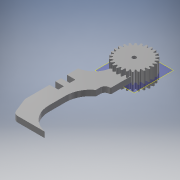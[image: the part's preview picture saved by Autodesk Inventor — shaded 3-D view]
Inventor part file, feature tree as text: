
AUTODESK INVENTOR PART (.ipt)
format: ipt  version: 2017 (Build 210142000, 142)  size: 346,624 bytes
history: native  units: mm (DEFAULTED — no unit token found)
features: plane x4, sketch x4, extrude x3, other x3
ambient origin geometry x8: Origin, YZ Plane, XZ Plane, XY Plane, X Axis, Y Axis, Z Axis, Center Point
bodies: Solid1 (feature_tree)
feature tree (14):
  extrude  "Extrusion1"  Depth=15.0mm TaperAngle=0.0deg
  plane  "Work Plane2"
  plane  "Work Plane8"
  plane  "Work Plane9"
  other  "Spur Gear"
  extrude  "Extrusion2"  Depth=10.0mm TaperAngle=0.0deg
  plane  "Work Plane11"
  extrude  "Extrusion4"  Depth=1.208305mm TaperAngle=0.0deg
  sketch  "Sketch1"  dims[d0=31.679524mm d1=15.0mm d2=0.0mm]
  sketch  "Sketch2"  dims[d3=29.433962mm d4=10.0mm d5=0.0mm]
  other  "Srf1"
  sketch  "Sketch3"  dims[d16=30.0mm d17=0.0mm d34=1.208305mm]
  sketch  "Sketch6"  dims[d39=0.0mm d41=0.0mm d43=30.0mm d46=30.0mm d47=0.0mm d48=0.0mm d49=3.5mm d50=20.0mm d51=0.0mm d88=-5.0mm d89=22.0mm d90=90.0deg d91=0.0mm d92=15.0mm d93=0.0mm d94=13.0mm d95=22.0mm d96=8.0mm d97=37.0mm d98=5.0mm d99=12.124057mm d100=5.2mm d101=5.2mm d102=5.0mm d103=17.0mm d104=4.0mm d105=90.0mm d106=8.0mm d107=15.0mm d108=1.0mm d109=27.628999mm d110=19.286438mm d111=7.5mm d112=53.562028mm d113=28.866465mm d114=1.328523mm d115=21.374169mm d116=17.412036mm d117=1.75mm d118=8.0mm d119=5.0mm d120=0.0mm]
  other  "Pitch Diameter"
